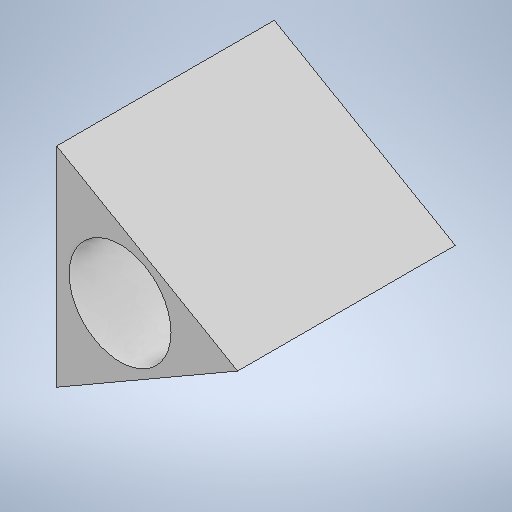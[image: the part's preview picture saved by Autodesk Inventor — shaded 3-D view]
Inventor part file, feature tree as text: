
AUTODESK INVENTOR PART (.ipt)
format: ipt  version: 2025.1 (Build 291241000, 241)  size: 204,800 bytes
history: native  units: mm
features: extrude x2, sketch x2
ambient origin geometry x8: Origin, YZ Plane, XZ Plane, XY Plane, X Axis, Y Axis, Z Axis, Center Point
bodies: Solid1 (feature_tree)
feature tree (4):
  extrude  "Extrusion1"  Depth=24.0mm
  extrude  "Extrusion2"  Depth=24.0mm
  sketch  "Sketch1"  dims[d3=25.0mm d4=0.0mm d7=24.0mm]
  sketch  "Sketch2"  dims[d8=24.0mm d9=24.0mm d10=11.7mm d11=13.5mm d12=0.0mm d13=10.0mm d14=0.0mm]
